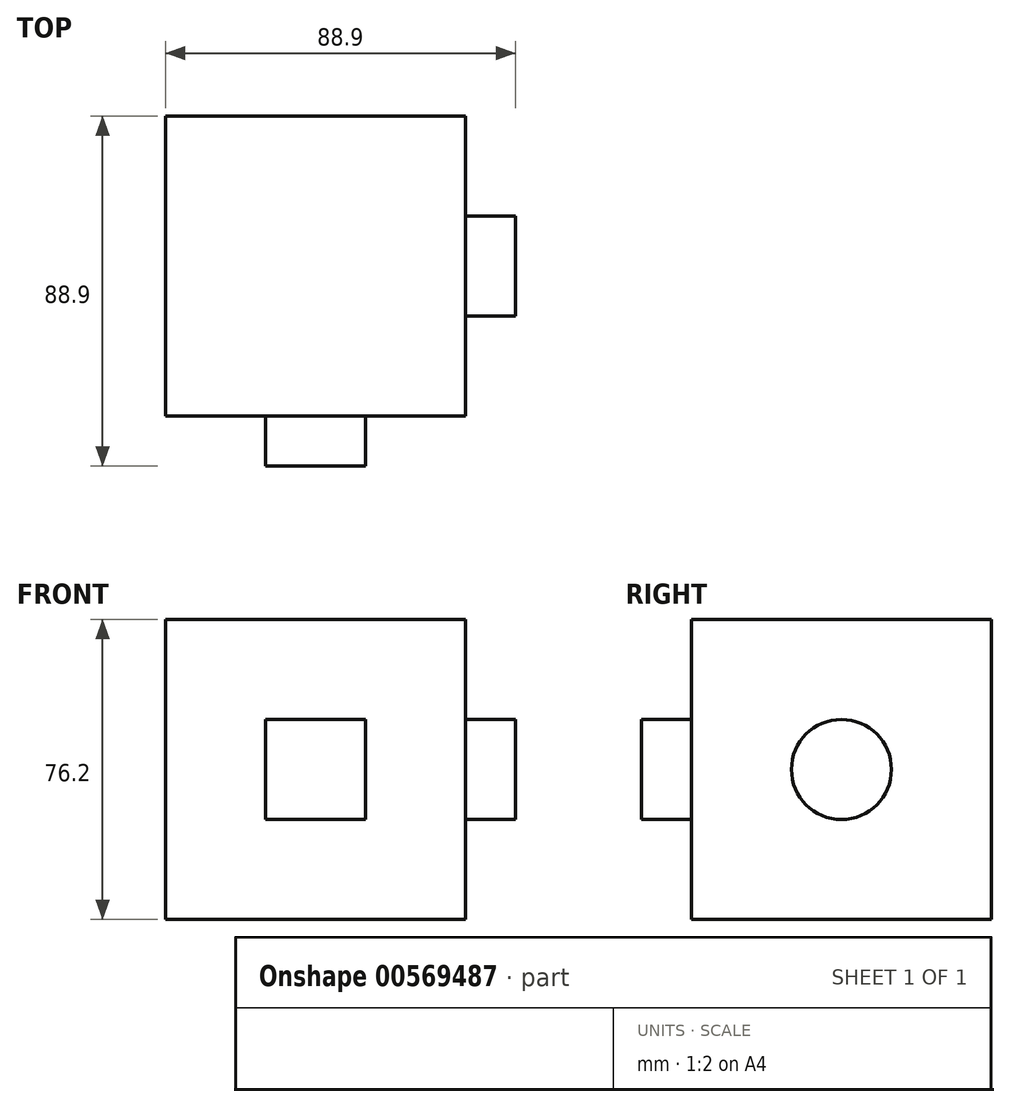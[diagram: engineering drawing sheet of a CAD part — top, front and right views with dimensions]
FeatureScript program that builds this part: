
annotation { "Feature Type Name" : "Feature", "Feature Type Description" : "" }
export const myFeature = defineFeature(function(context is Context, id is Id, definition is map)
    precondition{}
    {
        {
            var Q0;
            Q0=qCreatedBy(makeId("Front.planeOp"),FACE);
            var sketch = newSketch(context, id + "F0", { "sketchPlane" : qUnion([Q0])});
            skLineSegment(sketch, "E0.bottom", {"start": v(-58.86, 93.11) * mm, "end": v(17.34, 93.11) * mm});
            skLineSegment(sketch, "E0.top", {"start": v(-58.86, 16.91) * mm, "end": v(17.34, 16.91) * mm});
            skLineSegment(sketch, "E0.left", {"start": v(-58.86, 93.11) * mm, "end": v(-58.86, 16.91) * mm});
            skLineSegment(sketch, "E0.right", {"start": v(17.34, 93.11) * mm, "end": v(17.34, 16.91) * mm});
            skSolve(sketch);
        }
        {
            var Q0;
            Q0=makeQuery(id+"F0.imprint","IMPRINT",FACE,{"disambiguationData":[TD([[makeQuery(id+"F0.imprint","IMPRINT",EDGE,{"derivedFrom":sQuery(id+"F0.wireOp",EDGE,"E0.bottom")}),-1.0]])]});
            extrude(context, id + "F1", {"entities" : qUnion([Q0]), "depth" : 25.4 * mm, "offsetDistance" : 25.4 * mm});
        }
        {
            var Q0;
            Q0 = qSketchRegion(id + "F0", true);
            extrude(context, id + "F2", {"entities" : qUnion([Q0]), "operationType" : NewBodyOperationType.ADD, "depth" : 76.2 * mm, "offsetDistance" : 25.4 * mm});
        }
        {
            var Q0;
            Q0=makeQuery(id+"F2.opExtrude","CAP_FACE",FACE,{"disambiguationData":[OSD([sQuery(id+"F0.wireOp",EDGE,"E0.bottom"),sQuery(id+"F0.wireOp",EDGE,"E0.top"),sQuery(id+"F0.wireOp",EDGE,"E0.left"),sQuery(id+"F0.wireOp",EDGE,"E0.right")])],"isStart":false});
            var sketch = newSketch(context, id + "F3", { "sketchPlane" : qUnion([Q0])});
            skLineSegment(sketch, "E1.bottom", {"start": v(-33.46, 67.71) * mm, "end": v(-8.06, 67.71) * mm});
            skLineSegment(sketch, "E1.top", {"start": v(-33.46, 42.31) * mm, "end": v(-8.06, 42.31) * mm});
            skLineSegment(sketch, "E1.left", {"start": v(-33.46, 67.71) * mm, "end": v(-33.46, 42.31) * mm});
            skLineSegment(sketch, "E1.right", {"start": v(-8.06, 67.71) * mm, "end": v(-8.06, 42.31) * mm});
            skSolve(sketch);
        }
        {
            var Q0;
            Q0 = qSketchRegion(id + "F3", true);
            extrude(context, id + "F4", {"entities" : qUnion([Q0]), "operationType" : NewBodyOperationType.ADD, "depth" : 12.7 * mm, "offsetDistance" : 25.4 * mm});
        }
        {
            var Q0;
            {var subQ0=sQuery(id+"F0.wireOp",EDGE,"E0.right");Q0=makeQuery(id+"F2.boolean.opBoolean","MERGE",FACE,{"derivedFrom":[makeQuery(id+"F1.opExtrude","SWEPT_FACE",FACE,{"disambiguationData":[OSD([subQ0])]}),makeQuery(id+"F2.opExtrude","SWEPT_FACE",FACE,{"disambiguationData":[OSD([subQ0])]})]});}
            var sketch = newSketch(context, id + "F5", { "sketchPlane" : qUnion([Q0])});
            skCircle(sketch, "E2", {"center": v(-38.1, 55.01) * mm, "radius": 12.7 * mm});
            skSolve(sketch);
        }
        {
            var Q0;
            Q0 = qSketchRegion(id + "F5", true);
            extrude(context, id + "F6", {"entities" : qUnion([Q0]), "operationType" : NewBodyOperationType.ADD, "depth" : 12.7 * mm, "offsetDistance" : 25.4 * mm});
        }
    });
